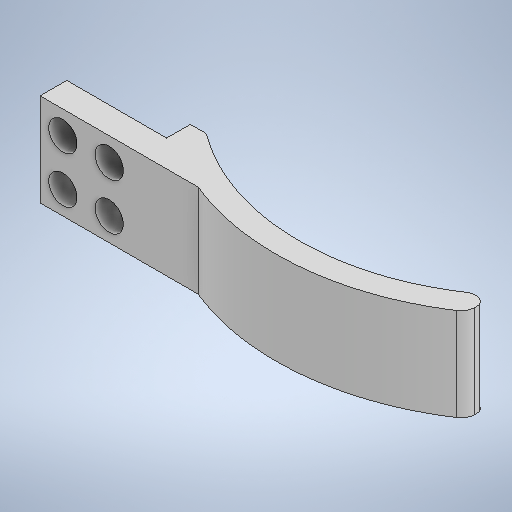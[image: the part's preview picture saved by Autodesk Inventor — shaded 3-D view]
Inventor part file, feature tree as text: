
AUTODESK INVENTOR PART (.ipt)
format: ipt  version: 2025.1 (Build 291241000, 241)  size: 276,992 bytes
history: native  units: mm
features: sketch x3, extrude x2, fillet x2
ambient origin geometry x8: Origin, YZ Plane, XZ Plane, XY Plane, X Axis, Y Axis, Z Axis, Center Point
bodies: Solid1 (feature_tree)
feature tree (7):
  extrude  "Extrusion1"  Depth=100.0mm
  fillet  "Fillet1"  Radius=4.999995mm
  fillet  "Fillet2"  Radius=20.0mm
  extrude  "Extrusion3"  Depth=2.5mm
  sketch  "Sketch1"  dims[d0=60.0mm d2=100.0mm d5=4.999995mm d6=20.0mm d7=0.0mm]
  sketch  "Sketch3"  dims[d23=1.428888mm d24=10.0mm d25=5.0mm d26=20.0mm d28=10.0mm d29=20.0mm d31=10.0mm d34=0.0mm d35=0.0mm]
  sketch  "Sketch Rectangular Pattern2"  dims[d21=3.0mm d22=2.5mm]
